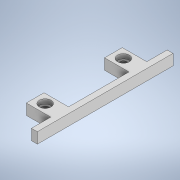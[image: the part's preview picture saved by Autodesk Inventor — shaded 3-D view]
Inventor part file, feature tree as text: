
AUTODESK INVENTOR PART (.ipt)
format: ipt  version: 2020 (Build 240168000, 168)  size: 138,752 bytes
history: native  units: mm
features: sketch x4, extrude x2, hole x2
ambient origin geometry x8: Origin, YZ Plane, XZ Plane, XY Plane, X Axis, Y Axis, Z Axis, Center Point
bodies: Solid1 (feature_tree)
feature tree (8):
  extrude  "Extrusion1"  Depth=69.0mm
  hole  "Hole1"  [1 undecoded]
  hole  "Hole2"  [1 undecoded]
  extrude  "Extrusion2"  Depth=9.0mm
  sketch  "Sketch1"  dims[d0=18.44mm d1=69.0mm]
  sketch  "Sketch4"  dims[d2=5.5mm d3=0.0mm d6=8.06mm]
  sketch  "Sketch5"  dims[d7=54.15mm]
  sketch  "Sketch6"  dims[d8=3.5mm d9=6.0mm d10=6.0mm d11=2.3mm d12=90.0deg d13=10.5mm d14=20.594885mm d15=8.06mm d16=14.35mm d17=3.5mm d18=6.0mm d19=6.0mm d20=2.3mm d21=90.0deg d22=10.5mm d23=20.594885mm d24=3.0mm d25=9.0mm d26=9.0mm d27=4.5mm d28=4.5mm d29=9.0mm d30=0.0mm d5=0.5mm]
note: 2 required parameter values undecoded (feature->parameter linkage not recoverable at this tier; creation-order binding heuristic only, values carry confidence <= 0.55)
